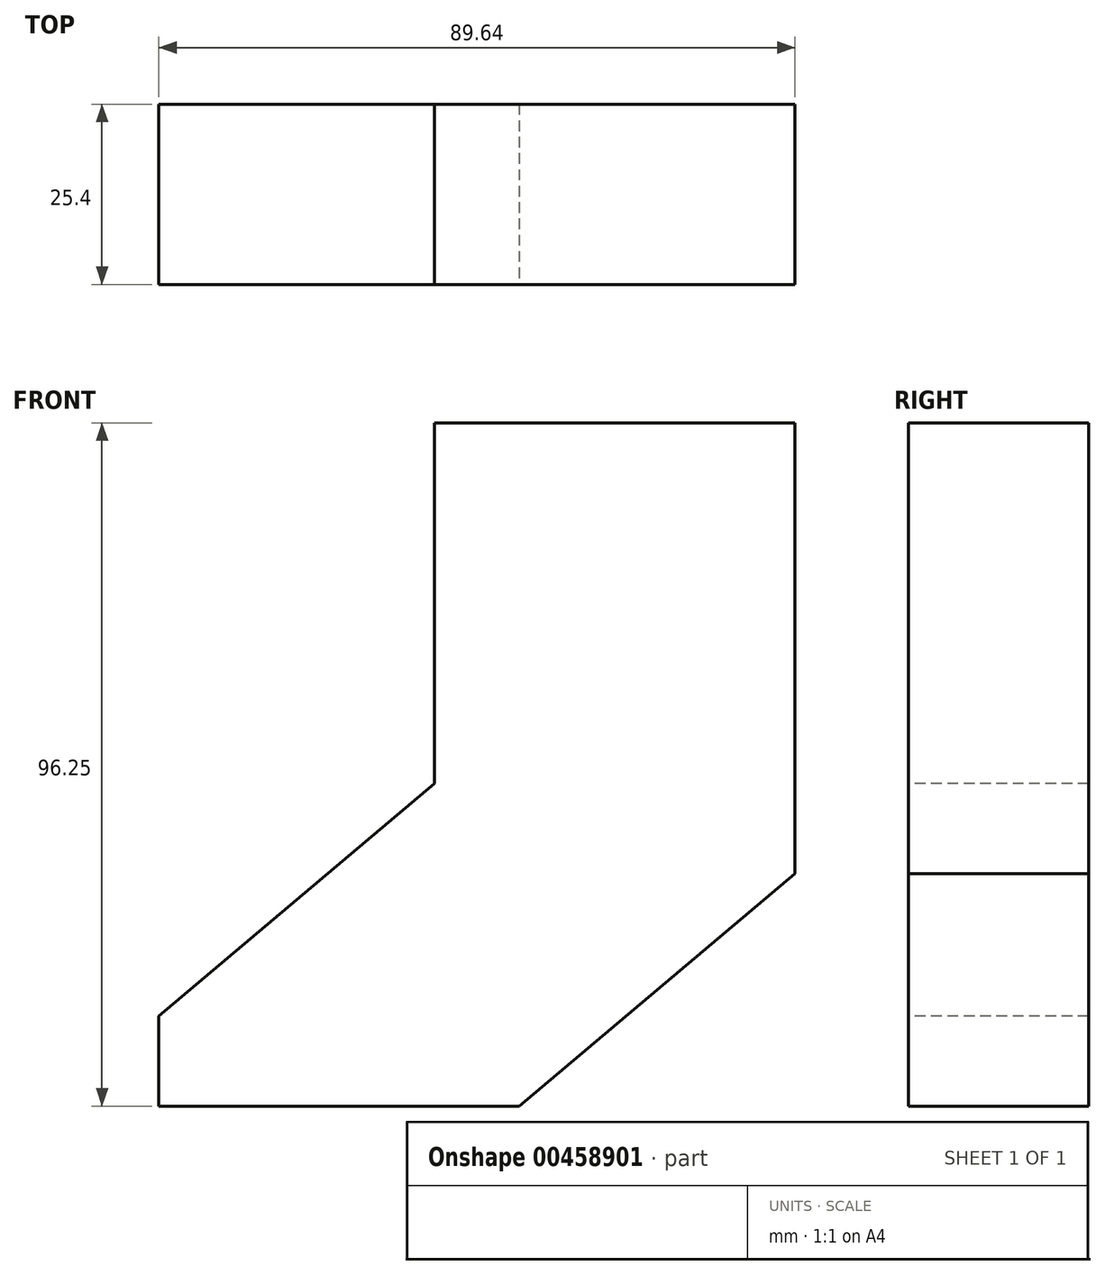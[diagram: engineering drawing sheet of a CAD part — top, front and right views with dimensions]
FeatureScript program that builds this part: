
annotation { "Feature Type Name" : "Feature", "Feature Type Description" : "" }
export const myFeature = defineFeature(function(context is Context, id is Id, definition is map)
    precondition{}
    {
        {
            var Q0;
            Q0=qCreatedBy(makeId("Front.planeOp"),FACE);
            var sketch = newSketch(context, id + "F0", { "sketchPlane" : qUnion([Q0])});
            skLineSegment(sketch, "E0.bottom", {"start": v(-48.96, 32.6) * mm, "end": v(1.84, 32.6) * mm});
            skLineSegment(sketch, "E0.top", {"start": v(-48.96, 19.9) * mm, "end": v(1.84, 19.9) * mm});
            skLineSegment(sketch, "E0.left", {"start": v(-48.96, 32.6) * mm, "end": v(-48.96, 19.9) * mm});
            skLineSegment(sketch, "E0.right", {"start": v(1.84, 32.6) * mm, "end": v(1.84, 19.9) * mm});
            skLineSegment(sketch, "E1", {"start": v(1.84, 32.6) * mm, "end": v(40.68, 65.34) * mm});
            skLineSegment(sketch, "E2", {"start": v(-48.96, 32.6) * mm, "end": v(-10.12, 65.34) * mm});
            skLineSegment(sketch, "E3", {"start": v(-10.12, 65.34) * mm, "end": v(-10.12, 116.14) * mm});
            skLineSegment(sketch, "E4", {"start": v(40.68, 65.34) * mm, "end": v(40.68, 116.14) * mm});
            skLineSegment(sketch, "E5", {"start": v(1.84, 19.9) * mm, "end": v(40.68, 52.64) * mm});
            skLineSegment(sketch, "E6", {"start": v(40.68, 52.64) * mm, "end": v(40.68, 65.34) * mm});
            skLineSegment(sketch, "E7", {"start": v(-48.96, 19.9) * mm, "end": v(-10.12, 52.64) * mm});
            skLineSegment(sketch, "E8", {"start": v(-10.12, 52.64) * mm, "end": v(-10.12, 65.34) * mm});
            skLineSegment(sketch, "E9", {"start": v(-10.12, 65.34) * mm, "end": v(40.68, 65.34) * mm});
            skLineSegment(sketch, "E10", {"start": v(40.68, 65.34) * mm, "end": v(40.68, 65.34) * mm});
            skLineSegment(sketch, "E11", {"start": v(40.68, 52.64) * mm, "end": v(-10.12, 52.64) * mm});
            skLineSegment(sketch, "E12", {"start": v(13.9, 140.08) * mm, "end": v(13.9, 139.87) * mm});
            skLineSegment(sketch, "E13", {"start": v(-10.12, 116.14) * mm, "end": v(40.68, 116.14) * mm});
            skSolve(sketch);
        }
        {
            var Q0;
            Q0 = qSketchRegion(id + "F0", true);
            var Q1;
            {var subQ1=sQuery(id+"F0.wireOp",EDGE,"E0.bottom");var subQ3=sQuery(id+"F0.wireOp",EDGE,"E7");var subQ4=makeQuery(id+"F0.imprint","INTERSECT",VERTEX,{"derivedFrom":[subQ1,subQ3]});Q1=makeQuery(id+"F0.imprint","IMPRINT",FACE,{"disambiguationData":[TD([[makeQuery(id+"F0.imprint","IMPRINT",EDGE,{"disambiguationData":[TD([[subQ4,-1.0]])],"derivedFrom":subQ1}),1.0]])]});}
            extrude(context, id + "F1", {"entities" : qUnion([Q0, Q1]), "oppositeDirection" : true, "depth" : 25.4 * mm});
        }
    });
